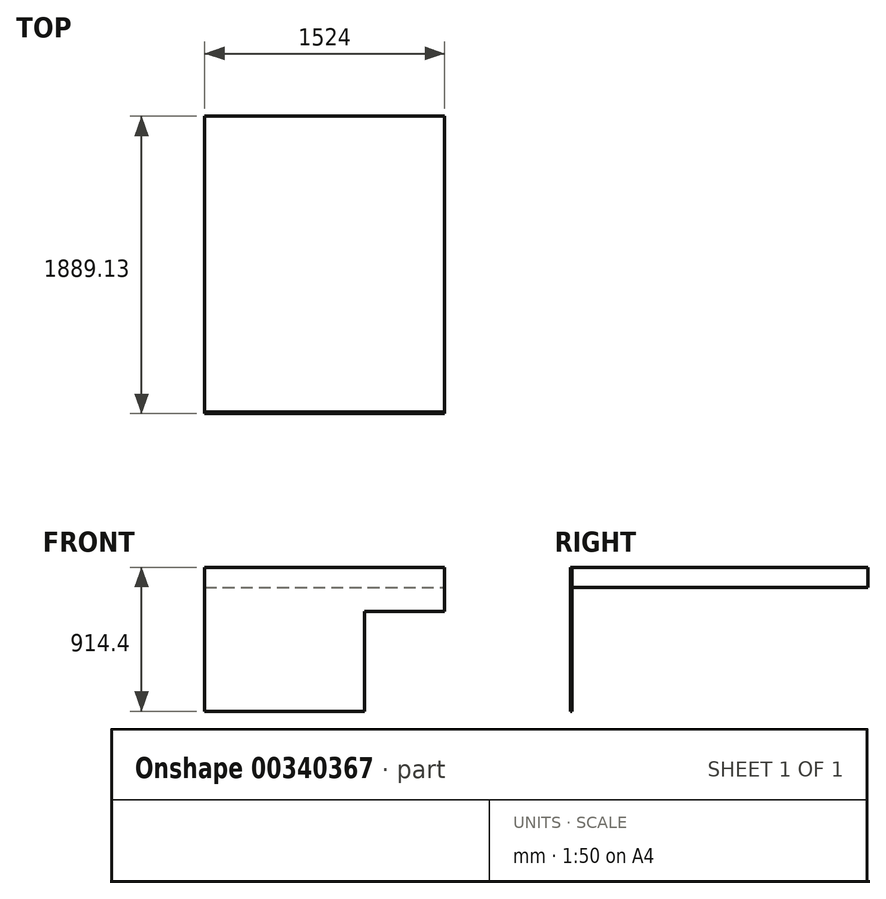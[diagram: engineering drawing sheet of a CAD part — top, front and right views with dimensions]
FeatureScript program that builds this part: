
annotation { "Feature Type Name" : "Feature", "Feature Type Description" : "" }
export const myFeature = defineFeature(function(context is Context, id is Id, definition is map)
    precondition{}
    {
        {
            var Q0;
            Q0=qCreatedBy(makeId("Front.planeOp"),FACE);
            var sketch = newSketch(context, id + "F0", { "sketchPlane" : qUnion([Q0])});
            skLineSegment(sketch, "E0.bottom", {"start": v(-762, 76.73) * mm, "end": v(762, 76.73) * mm});
            skLineSegment(sketch, "E0.top", {"start": v(-762, -50.27) * mm, "end": v(762, -50.27) * mm});
            skLineSegment(sketch, "E0.left", {"start": v(-762, 76.73) * mm, "end": v(-762, -50.27) * mm});
            skLineSegment(sketch, "E0.right", {"start": v(762, 76.73) * mm, "end": v(762, -50.27) * mm});
            skPoint(sketch, "E0.middle", {"position": v(0, 13.23) * mm});
            skSolve(sketch);
        }
        {
            var Q0;
            Q0=makeQuery(id+"F0.imprint","IMPRINT",FACE,{"disambiguationData":[TD([[makeQuery(id+"F0.imprint","IMPRINT",EDGE,{"derivedFrom":sQuery(id+"F0.wireOp",EDGE,"E0.bottom")}),-1.0]])]});
            extrude(context, id + "F1", {"entities" : qUnion([Q0]), "oppositeDirection" : true, "depth" : 1879.6 * mm});
        }
        {
            var Q0;
            Q0=makeQuery(id+"F1.opExtrude","CAP_FACE",FACE,{"disambiguationData":[OSD([sQuery(id+"F0.wireOp",EDGE,"E0.bottom"),sQuery(id+"F0.wireOp",EDGE,"E0.top"),sQuery(id+"F0.wireOp",EDGE,"E0.left"),sQuery(id+"F0.wireOp",EDGE,"E0.right")])],"isStart":true});
            var sketch = newSketch(context, id + "F2", { "sketchPlane" : qUnion([Q0])});
            skLineSegment(sketch, "E1.bottom", {"start": v(-762, 76.73) * mm, "end": v(762, 76.73) * mm});
            skLineSegment(sketch, "E1.top", {"start": v(-762, -837.67) * mm, "end": v(762, -837.67) * mm});
            skLineSegment(sketch, "E1.left", {"start": v(-762, 76.73) * mm, "end": v(-762, -837.67) * mm});
            skLineSegment(sketch, "E1.right", {"start": v(762, 76.73) * mm, "end": v(762, -837.67) * mm});
            skSolve(sketch);
        }
        {
            var Q0;
            Q0 = qSketchRegion(id + "F2", true);
            extrude(context, id + "F3", {"entities" : qUnion([Q0]), "depth" : 9.52 * mm});
        }
        {
            var Q0;
            Q0=makeQuery(id+"F3.opExtrude","CAP_FACE",FACE,{"disambiguationData":[OSD([sQuery(id+"F2.wireOp",EDGE,"E1.bottom"),sQuery(id+"F2.wireOp",EDGE,"E1.top"),sQuery(id+"F2.wireOp",EDGE,"E1.left"),sQuery(id+"F2.wireOp",EDGE,"E1.right")])],"isStart":false});
            var sketch = newSketch(context, id + "F4", { "sketchPlane" : qUnion([Q0])});
            skLineSegment(sketch, "E2.bottom", {"start": v(762, -837.67) * mm, "end": v(254, -837.67) * mm});
            skLineSegment(sketch, "E2.top", {"start": v(762, -202.67) * mm, "end": v(254, -202.67) * mm});
            skLineSegment(sketch, "E2.left", {"start": v(762, -837.67) * mm, "end": v(762, -202.67) * mm});
            skLineSegment(sketch, "E2.right", {"start": v(254, -837.67) * mm, "end": v(254, -202.67) * mm});
            skSolve(sketch);
        }
        {
            var Q0;
            Q0 = qSketchRegion(id + "F4", true);
            extrude(context, id + "F5", {"entities" : qUnion([Q0]), "operationType" : NewBodyOperationType.REMOVE, "oppositeDirection" : true, "depth" : 19.05 * mm});
        }
    });
